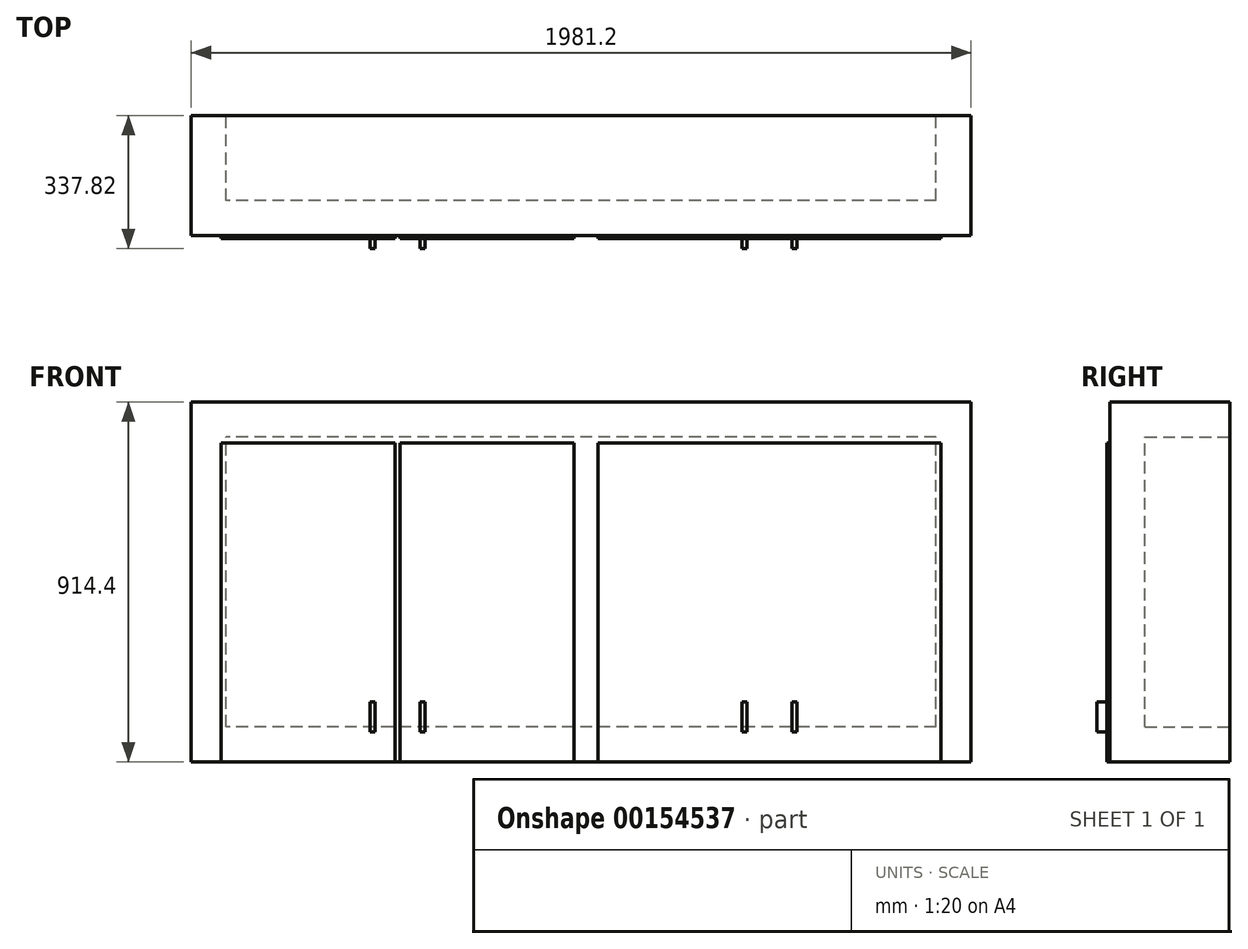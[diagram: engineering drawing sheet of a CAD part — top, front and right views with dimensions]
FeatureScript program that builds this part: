
annotation { "Feature Type Name" : "Feature", "Feature Type Description" : "" }
export const myFeature = defineFeature(function(context is Context, id is Id, definition is map)
    precondition{}
    {
        {
            var Q0;
            Q0=qCreatedBy(makeId("Front.planeOp"),FACE);
            var sketch = newSketch(context, id + "F0", { "sketchPlane" : qUnion([Q0])});
            skLineSegment(sketch, "E0.bottom", {"start": v(0, 0) * mm, "end": v(1981.2, 0) * mm});
            skLineSegment(sketch, "E0.top", {"start": v(0, 914.4) * mm, "end": v(1981.2, 914.4) * mm});
            skLineSegment(sketch, "E0.left", {"start": v(0, 0) * mm, "end": v(0, 914.4) * mm});
            skLineSegment(sketch, "E0.right", {"start": v(1981.2, 0) * mm, "end": v(1981.2, 914.4) * mm});
            skSolve(sketch);
        }
        {
            var Q0;
            Q0=makeQuery(id+"F0.imprint","IMPRINT",FACE,{"disambiguationData":[TD([[makeQuery(id+"F0.imprint","IMPRINT",EDGE,{"derivedFrom":sQuery(id+"F0.wireOp",EDGE,"E0.bottom")}),1.0]])]});
            extrude(context, id + "F1", {"entities" : qUnion([Q0]), "oppositeDirection" : true, "depth" : 304.8 * mm});
        }
        {
            var Q0;
            Q0=makeQuery(id+"F1.opExtrude","CAP_FACE",FACE,{"disambiguationData":[OSD([sQuery(id+"F0.wireOp",EDGE,"E0.bottom"),sQuery(id+"F0.wireOp",EDGE,"E0.top"),sQuery(id+"F0.wireOp",EDGE,"E0.left"),sQuery(id+"F0.wireOp",EDGE,"E0.right")])],"isStart":true});
            var sketch = newSketch(context, id + "F2", { "sketchPlane" : qUnion([Q0])});
            skLineSegment(sketch, "E1.bottom", {"start": v(76.2, 810.77) * mm, "end": v(518.16, 810.77) * mm});
            skLineSegment(sketch, "E1.top", {"start": v(76.2, 0) * mm, "end": v(518.16, 0) * mm});
            skLineSegment(sketch, "E1.left", {"start": v(76.2, 810.77) * mm, "end": v(76.2, 0) * mm});
            skLineSegment(sketch, "E1.right", {"start": v(518.16, 810.77) * mm, "end": v(518.16, 0) * mm});
            skLineSegment(sketch, "E2.bottom", {"start": v(530.86, 0) * mm, "end": v(972.82, 0) * mm});
            skLineSegment(sketch, "E2.top", {"start": v(530.86, 810.77) * mm, "end": v(972.82, 810.77) * mm});
            skLineSegment(sketch, "E2.left", {"start": v(530.86, 0) * mm, "end": v(530.86, 810.77) * mm});
            skLineSegment(sketch, "E2.right", {"start": v(972.82, 0) * mm, "end": v(972.82, 810.77) * mm});
            skLineSegment(sketch, "E3.bottom", {"start": v(1033.78, 0) * mm, "end": v(1475.74, 0) * mm});
            skLineSegment(sketch, "E3.top", {"start": v(1033.78, 810.77) * mm, "end": v(1475.74, 810.77) * mm});
            skLineSegment(sketch, "E3.left", {"start": v(1033.78, 0) * mm, "end": v(1033.78, 810.77) * mm});
            skLineSegment(sketch, "E3.right", {"start": v(1475.74, 0) * mm, "end": v(1475.74, 810.77) * mm});
            skLineSegment(sketch, "E4.bottom", {"start": v(1463.04, 0) * mm, "end": v(1905, 0) * mm});
            skLineSegment(sketch, "E4.top", {"start": v(1463.04, 810.77) * mm, "end": v(1905, 810.77) * mm});
            skLineSegment(sketch, "E4.left", {"start": v(1463.04, 0) * mm, "end": v(1463.04, 810.77) * mm});
            skLineSegment(sketch, "E4.right", {"start": v(1905, 0) * mm, "end": v(1905, 810.77) * mm});
            skSolve(sketch);
        }
        {
            var Q0;
            Q0=makeQuery(id+"F2.imprint","IMPRINT",FACE,{"disambiguationData":[TD([[makeQuery(id+"F2.imprint","IMPRINT",EDGE,{"derivedFrom":sQuery(id+"F2.wireOp",EDGE,"E1.bottom")}),-1.0]])]});
            var Q1;
            Q1=makeQuery(id+"F2.imprint","IMPRINT",FACE,{"disambiguationData":[TD([[makeQuery(id+"F2.imprint","IMPRINT",EDGE,{"derivedFrom":sQuery(id+"F2.wireOp",EDGE,"E2.bottom")}),1.0]])]});
            var Q2;
            Q2=makeQuery(id+"F2.imprint","IMPRINT",FACE,{"disambiguationData":[TD([[makeQuery(id+"F2.imprint","IMPRINT",EDGE,{"derivedFrom":sQuery(id+"F2.wireOp",EDGE,"E3.bottom")}),1.0]])]});
            var Q3;
            {var subQ0=sQuery(id+"F2.wireOp",EDGE,"E3.right");Q3=makeQuery(id+"F2.imprint","IMPRINT",FACE,{"disambiguationData":[TD([[makeQuery(id+"F2.imprint","IMPRINT",EDGE,{"derivedFrom":subQ0}),-1.0]])]});}
            extrude(context, id + "F3", {"entities" : qUnion([Q0, Q1, Q2, Q3]), "operationType" : NewBodyOperationType.ADD, "depth" : 7.62 * mm});
        }
        {
            var Q0;
            Q0=makeQuery(id+"F3.opExtrude","CAP_FACE",FACE,{"disambiguationData":[OSD([sQuery(id+"F2.wireOp",EDGE,"E1.bottom"),sQuery(id+"F2.wireOp",EDGE,"E1.top"),sQuery(id+"F2.wireOp",EDGE,"E1.left"),sQuery(id+"F2.wireOp",EDGE,"E1.right")])],"isStart":false});
            var sketch = newSketch(context, id + "F4", { "sketchPlane" : qUnion([Q0])});
            skLineSegment(sketch, "E5.bottom", {"start": v(454.66, 152.4) * mm, "end": v(467.36, 152.4) * mm});
            skLineSegment(sketch, "E5.top", {"start": v(454.66, 76.2) * mm, "end": v(467.36, 76.2) * mm});
            skLineSegment(sketch, "E5.left", {"start": v(454.66, 152.4) * mm, "end": v(454.66, 76.2) * mm});
            skLineSegment(sketch, "E5.right", {"start": v(467.36, 152.4) * mm, "end": v(467.36, 76.2) * mm});
            skLineSegment(sketch, "E6.bottom", {"start": v(581.66, 152.4) * mm, "end": v(594.36, 152.4) * mm});
            skLineSegment(sketch, "E6.top", {"start": v(581.66, 76.2) * mm, "end": v(594.36, 76.2) * mm});
            skLineSegment(sketch, "E6.left", {"start": v(581.66, 152.4) * mm, "end": v(581.66, 76.2) * mm});
            skLineSegment(sketch, "E6.right", {"start": v(594.36, 152.4) * mm, "end": v(594.36, 76.2) * mm});
            skLineSegment(sketch, "E7.bottom", {"start": v(1399.54, 152.4) * mm, "end": v(1412.24, 152.4) * mm});
            skLineSegment(sketch, "E7.top", {"start": v(1399.54, 76.2) * mm, "end": v(1412.24, 76.2) * mm});
            skLineSegment(sketch, "E7.left", {"start": v(1399.54, 152.4) * mm, "end": v(1399.54, 76.2) * mm});
            skLineSegment(sketch, "E7.right", {"start": v(1412.24, 152.4) * mm, "end": v(1412.24, 76.2) * mm});
            skLineSegment(sketch, "E8.bottom", {"start": v(1526.54, 152.4) * mm, "end": v(1539.24, 152.4) * mm});
            skLineSegment(sketch, "E8.top", {"start": v(1526.54, 76.2) * mm, "end": v(1539.24, 76.2) * mm});
            skLineSegment(sketch, "E8.left", {"start": v(1526.54, 152.4) * mm, "end": v(1526.54, 76.2) * mm});
            skLineSegment(sketch, "E8.right", {"start": v(1539.24, 152.4) * mm, "end": v(1539.24, 76.2) * mm});
            skLineSegment(sketch, "E9", {"start": v(467.36, 114.3) * mm, "end": v(518.16, 114.3) * mm, "construction": true});
            skLineSegment(sketch, "E10", {"start": v(530.86, 114.3) * mm, "end": v(581.66, 114.3) * mm, "construction": true});
            skLineSegment(sketch, "E11", {"start": v(1412.24, 114.3) * mm, "end": v(1463.04, 114.3) * mm, "construction": true});
            skLineSegment(sketch, "E12", {"start": v(1475.74, 114.3) * mm, "end": v(1526.54, 114.3) * mm, "construction": true});
            skSolve(sketch);
        }
        {
            var Q0;
            Q0=makeQuery(id+"F4.imprint","IMPRINT",FACE,{"disambiguationData":[TD([[makeQuery(id+"F4.imprint","IMPRINT",EDGE,{"derivedFrom":sQuery(id+"F4.wireOp",EDGE,"E8.bottom")}),-1.0]])]});
            var Q1;
            Q1=makeQuery(id+"F4.imprint","IMPRINT",FACE,{"disambiguationData":[TD([[makeQuery(id+"F4.imprint","IMPRINT",EDGE,{"derivedFrom":sQuery(id+"F4.wireOp",EDGE,"E7.bottom")}),-1.0]])]});
            var Q2;
            Q2=makeQuery(id+"F4.imprint","IMPRINT",FACE,{"disambiguationData":[TD([[makeQuery(id+"F4.imprint","IMPRINT",EDGE,{"derivedFrom":sQuery(id+"F4.wireOp",EDGE,"E6.bottom")}),-1.0]])]});
            var Q3;
            Q3=makeQuery(id+"F4.imprint","IMPRINT",FACE,{"disambiguationData":[TD([[makeQuery(id+"F4.imprint","IMPRINT",EDGE,{"derivedFrom":sQuery(id+"F4.wireOp",EDGE,"E5.bottom")}),-1.0]])]});
            extrude(context, id + "F5", {"entities" : qUnion([Q0, Q1, Q2, Q3]), "operationType" : NewBodyOperationType.ADD, "depth" : 25.4 * mm});
        }
        {
            var Q0;
            Q0=makeQuery(id+"F1.opExtrude","CAP_FACE",FACE,{"disambiguationData":[OSD([sQuery(id+"F0.wireOp",EDGE,"E0.bottom"),sQuery(id+"F0.wireOp",EDGE,"E0.top"),sQuery(id+"F0.wireOp",EDGE,"E0.left"),sQuery(id+"F0.wireOp",EDGE,"E0.right")])],"isStart":false});
            var sketch = newSketch(context, id + "F6", { "sketchPlane" : qUnion([Q0])});
            skLineSegment(sketch, "E13.bottom", {"start": v(-1892.3, 88.9) * mm, "end": v(-88.9, 88.9) * mm});
            skLineSegment(sketch, "E13.top", {"start": v(-1892.3, 825.5) * mm, "end": v(-88.9, 825.5) * mm});
            skLineSegment(sketch, "E13.left", {"start": v(-1892.3, 88.9) * mm, "end": v(-1892.3, 825.5) * mm});
            skLineSegment(sketch, "E13.right", {"start": v(-88.9, 88.9) * mm, "end": v(-88.9, 825.5) * mm});
            skSolve(sketch);
        }
        {
            var Q0;
            Q0=makeQuery(id+"F6.imprint","IMPRINT",FACE,{"disambiguationData":[TD([[makeQuery(id+"F6.imprint","IMPRINT",EDGE,{"derivedFrom":sQuery(id+"F6.wireOp",EDGE,"E13.bottom")}),1.0]])]});
            extrude(context, id + "F7", {"entities" : qUnion([Q0]), "operationType" : NewBodyOperationType.REMOVE, "oppositeDirection" : true, "depth" : 215.9 * mm});
        }
    });
